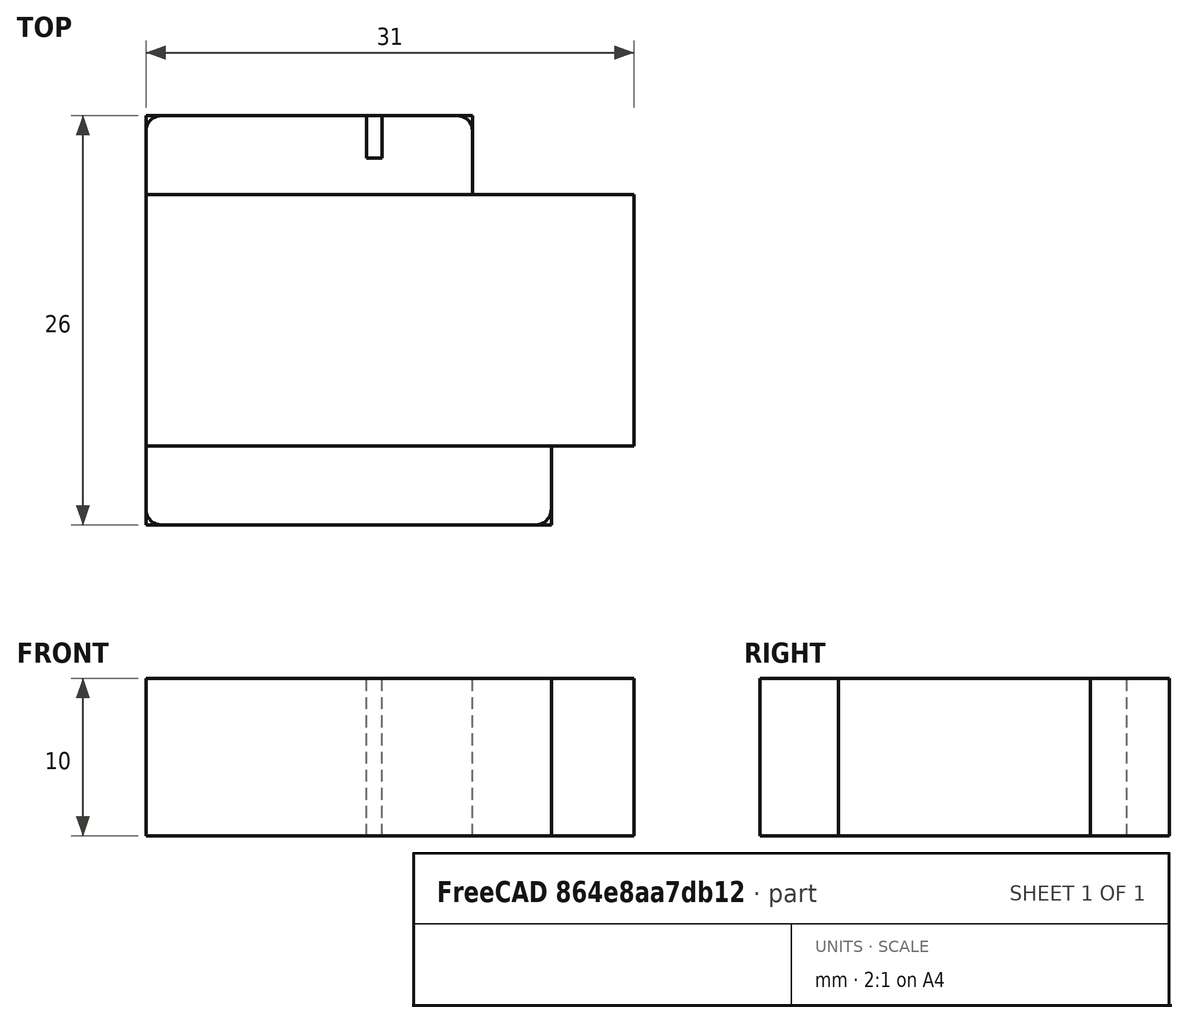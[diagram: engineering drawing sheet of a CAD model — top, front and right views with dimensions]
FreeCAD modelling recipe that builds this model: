
FCSTD DOCUMENT  (FreeCAD 0.15R4671 (Git))
Label: IntelliServoOutline
License: All rights reserved
LicenseURL: http://en.wikipedia.org/wiki/All_rights_reserved
objects: Part::Box×4, Part::MultiFuse×1, Part::Cut×1, PartDesign::Fillet×1, Part::Part2DObjectPython×1
note: 8 computed .brp shape members not serialized (recipe doc carries the construction recipe); baked Part::Feature solids carry a one-line shape summary decoded from their .brp

FEATURE [Part::Box] Box  label="Cube"
  Height = 10
  Length = 31
  Width = 16
FEATURE [Part::Box] Box001  label="Cube001"
  Height = 10
  Length = 20.75
  Placement = pos=(0,16,0) rot=(0,0,1;0rad)
  Width = 5
FEATURE [Part::Box] Box002  label="Cube002"
  Height = 10
  Length = 25.75
  Placement = pos=(0,-5,0) rot=(0,0,1;0rad)
  Width = 5
FEATURE [Part::MultiFuse] Fusion
  Shapes = -> [Box,Box001,Box002]
FEATURE [Part::Box] Box003  label="Cube003"
  Height = 10
  Length = 1
  Placement = pos=(14,18.3,0) rot=(0,0,1;0rad)
  Width = 2.7
FEATURE [Part::Cut] Cut
  Base = -> Fusion
  Tool = -> Box003
FEATURE [PartDesign::Fillet] Fillet
  Base = -> Cut [Edge4,Edge2,Edge37,Edge32]
  Radius = 1
FEATURE [Part::Part2DObjectPython] Shape2DView  # Draft 2D object (typed FeaturePython)
  Base = -> Fillet
  HiddenLines = false
  Projection = (0,0,1)
  ProjectionMode = 0
  SegmentLength = 0.05
  Tessellation = false
